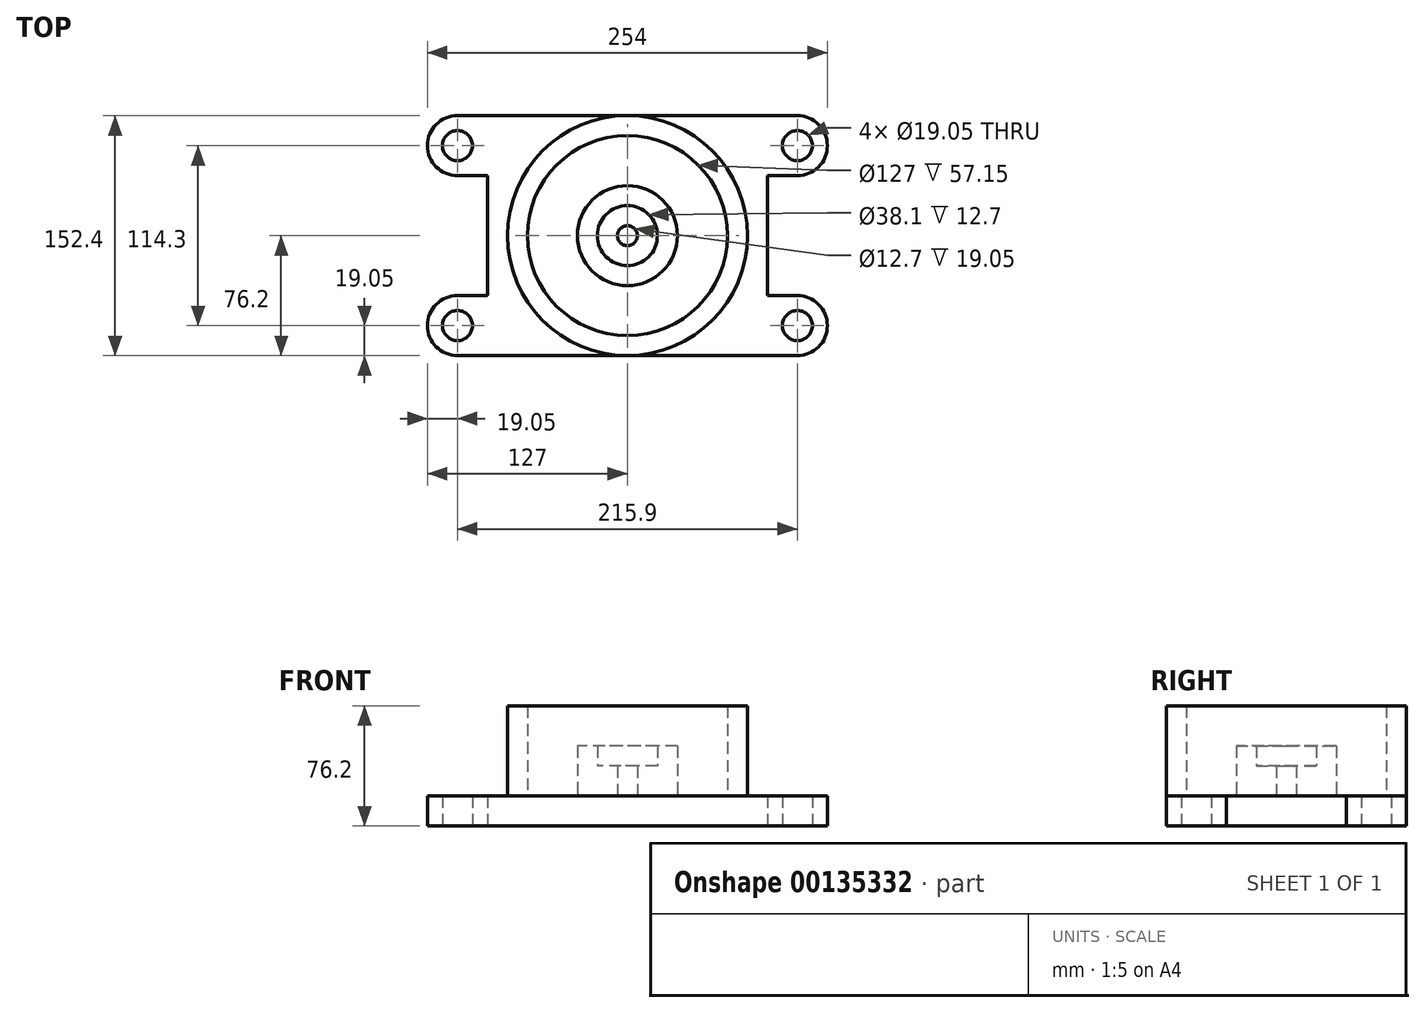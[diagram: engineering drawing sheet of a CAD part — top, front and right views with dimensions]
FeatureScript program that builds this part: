
annotation { "Feature Type Name" : "Feature", "Feature Type Description" : "" }
export const myFeature = defineFeature(function(context is Context, id is Id, definition is map)
    precondition{}
    {
        {
            var Q0;
            Q0=qCreatedBy(makeId("Top.planeOp"),FACE);
            var sketch = newSketch(context, id + "F0", { "sketchPlane" : qUnion([Q0])});
            skCircle(sketch, "E0", {"center": v(0, 0) * mm, "radius": 6.35 * mm});
            skCircle(sketch, "E1", {"center": v(0, 0) * mm, "radius": 19.05 * mm});
            skCircle(sketch, "E2", {"center": v(0, 0) * mm, "radius": 63.5 * mm});
            skCircle(sketch, "E3", {"center": v(0, 0) * mm, "radius": 76.2 * mm});
            skCircle(sketch, "E4", {"center": v(0, 0) * mm, "radius": 31.75 * mm});
            skLineSegment(sketch, "E5", {"start": v(0, -76.2) * mm, "end": v(-107.95, -76.2) * mm});
            skArc(sketch, "E6", {"start": v(-107.95, -38.1) * mm, "mid": v(-127, -57.15) * mm, "end": v(-107.95, -76.2) * mm});
            skCircle(sketch, "E7", {"center": v(-107.95, -57.15) * mm, "radius": 9.53 * mm});
            skLineSegment(sketch, "E8", {"start": v(0, 76.2) * mm, "end": v(107.95, 76.2) * mm});
            skArc(sketch, "E9", {"start": v(107.95, 38.1) * mm, "mid": v(127, 57.15) * mm, "end": v(107.95, 76.2) * mm});
            skCircle(sketch, "E10", {"center": v(107.95, 57.15) * mm, "radius": 9.53 * mm});
            skLineSegment(sketch, "E11", {"start": v(88.9, 0) * mm, "end": v(88.9, 38.1) * mm});
            skLineSegment(sketch, "E12", {"start": v(88.9, 38.1) * mm, "end": v(107.95, 38.1) * mm});
            skLineSegment(sketch, "E13", {"start": v(76.2, 0) * mm, "end": v(88.9, 0) * mm});
            skLineSegment(sketch, "E14", {"start": v(107.95, 57.15) * mm, "end": v(88.9, 57.15) * mm, "construction": true});
            skLineSegment(sketch, "E15", {"start": v(-107.95, -38.1) * mm, "end": v(-88.9, -38.1) * mm});
            skLineSegment(sketch, "E16", {"start": v(-88.9, -38.1) * mm, "end": v(-88.9, 0) * mm});
            skLineSegment(sketch, "E17", {"start": v(-88.9, 0) * mm, "end": v(-76.2, 0) * mm});
            skLineSegment(sketch, "E18", {"start": v(-107.95, -57.15) * mm, "end": v(-88.9, -57.15) * mm, "construction": true});
            skLineSegment(sketch, "E19.MirrorCS", {"start": v(-88.9, 38.1) * mm, "end": v(-88.9, 0) * mm});
            skLineSegment(sketch, "E20.MirrorCS", {"start": v(-107.95, 38.1) * mm, "end": v(-88.9, 38.1) * mm});
            skArc(sketch, "E21.MirrorCS", {"start": v(-107.95, 38.1) * mm, "mid": v(-127, 57.15) * mm, "end": v(-107.95, 76.2) * mm});
            skCircle(sketch, "E22.MirrorC", {"center": v(-107.95, 57.15) * mm, "radius": 9.53 * mm});
            skLineSegment(sketch, "E23.MirrorCS", {"start": v(0, 76.2) * mm, "end": v(-107.95, 76.2) * mm});
            skLineSegment(sketch, "E24.MirrorCS", {"start": v(88.9, 0) * mm, "end": v(88.9, -38.1) * mm});
            skLineSegment(sketch, "E25.MirrorCS", {"start": v(88.9, -38.1) * mm, "end": v(107.95, -38.1) * mm});
            skArc(sketch, "E26.MirrorCS", {"start": v(107.95, -38.1) * mm, "mid": v(127, -57.15) * mm, "end": v(107.95, -76.2) * mm});
            skCircle(sketch, "E27.MirrorC", {"center": v(107.95, -57.15) * mm, "radius": 9.53 * mm});
            skLineSegment(sketch, "E28.MirrorCS", {"start": v(0, -76.2) * mm, "end": v(107.95, -76.2) * mm});
            skSolve(sketch);
        }
        {
            var Q0;
            {var subQ1=sQuery(id+"F0.wireOp",EDGE,"E8");Q0=makeQuery(id+"F0.imprint","IMPRINT",FACE,{"disambiguationData":[TD([[makeQuery(id+"F0.imprint","IMPRINT",EDGE,{"derivedFrom":subQ1}),-1.0]])]});}
            var Q1;
            {var subQ0=sQuery(id+"F0.wireOp",EDGE,"E17");Q1=makeQuery(id+"F0.imprint","IMPRINT",FACE,{"disambiguationData":[TD([[makeQuery(id+"F0.imprint","IMPRINT",EDGE,{"derivedFrom":subQ0}),1.0]])]});}
            var Q2;
            {var subQ0=sQuery(id+"F0.wireOp",EDGE,"E5");Q2=makeQuery(id+"F0.imprint","IMPRINT",FACE,{"disambiguationData":[TD([[makeQuery(id+"F0.imprint","IMPRINT",EDGE,{"derivedFrom":subQ0}),-1.0]])]});}
            var Q3;
            {var subQ0=sQuery(id+"F0.wireOp",EDGE,"E13");Q3=makeQuery(id+"F0.imprint","IMPRINT",FACE,{"disambiguationData":[TD([[makeQuery(id+"F0.imprint","IMPRINT",EDGE,{"derivedFrom":subQ0}),-1.0]])]});}
            var Q4;
            Q4=makeQuery(id+"F0.imprint","IMPRINT",FACE,{"disambiguationData":[TD([[makeQuery(id+"F0.imprint","IMPRINT",EDGE,{"derivedFrom":sQuery(id+"F0.wireOp",EDGE,"E2")}),-1.0]])]});
            var Q5;
            Q5=makeQuery(id+"F0.imprint","IMPRINT",FACE,{"disambiguationData":[TD([[makeQuery(id+"F0.imprint","IMPRINT",EDGE,{"derivedFrom":sQuery(id+"F0.wireOp",EDGE,"E2")}),1.0]])]});
            var Q6;
            Q6=makeQuery(id+"F0.imprint","IMPRINT",FACE,{"disambiguationData":[TD([[makeQuery(id+"F0.imprint","IMPRINT",EDGE,{"derivedFrom":sQuery(id+"F0.wireOp",EDGE,"E1")}),-1.0]])]});
            var Q7;
            Q7=makeQuery(id+"F0.imprint","IMPRINT",FACE,{"disambiguationData":[TD([[makeQuery(id+"F0.imprint","IMPRINT",EDGE,{"derivedFrom":sQuery(id+"F0.wireOp",EDGE,"E0")}),-1.0]])]});
            var Q8;
            Q8=makeQuery(id+"F0.imprint","IMPRINT",FACE,{"disambiguationData":[TD([[makeQuery(id+"F0.imprint","IMPRINT",EDGE,{"derivedFrom":sQuery(id+"F0.wireOp",EDGE,"E0")}),1.0]])]});
            extrude(context, id + "F1", {"entities" : qUnion([Q0, Q1, Q2, Q3, Q4, Q5, Q6, Q7, Q8]), "depth" : 19.05 * mm});
        }
        {
            var Q0;
            Q0=makeQuery(id+"F0.imprint","IMPRINT",FACE,{"disambiguationData":[TD([[makeQuery(id+"F0.imprint","IMPRINT",EDGE,{"derivedFrom":sQuery(id+"F0.wireOp",EDGE,"E2")}),-1.0]])]});
            extrude(context, id + "F2", {"entities" : qUnion([Q0]), "operationType" : NewBodyOperationType.ADD, "depth" : 76.2 * mm});
        }
        {
            var Q0;
            Q0=makeQuery(id+"F0.imprint","IMPRINT",FACE,{"disambiguationData":[TD([[makeQuery(id+"F0.imprint","IMPRINT",EDGE,{"derivedFrom":sQuery(id+"F0.wireOp",EDGE,"E1")}),-1.0]])]});
            extrude(context, id + "F3", {"entities" : qUnion([Q0]), "operationType" : NewBodyOperationType.ADD, "depth" : 50.8 * mm});
        }
        {
            var Q0;
            Q0=makeQuery(id+"F0.imprint","IMPRINT",FACE,{"disambiguationData":[TD([[makeQuery(id+"F0.imprint","IMPRINT",EDGE,{"derivedFrom":sQuery(id+"F0.wireOp",EDGE,"E0")}),-1.0]])]});
            extrude(context, id + "F4", {"entities" : qUnion([Q0]), "operationType" : NewBodyOperationType.ADD, "depth" : 38.1 * mm});
        }
    });
